# Revit family: HERZ-Herzcules-Thermostatkopf M28x1.5 9860
name_source: partatom
category: Rohrzubehör
units: mm (PartAtom-declared; Revit-internal decimal feet)

## family parameters
Arbeitsebenenbasiert = Nein
Beim Laden mit Abzugskörper schneiden = Nein
Bemaßung runder Anschluss = Durchmesser verwenden
Gemeinsam genutzt = Nein
Immer vertikal = Nein
OmniClass-Nummer = 23.65.55.14
OmniClass-Titel = Valves for Liquid Services
Teiletyp = Normal

## types (1)
- HERZ-Herzcules-Thermostatkopf M28x1.5 9860
    Anwendungen = HERZCULES, Thermostatkopf zur Montage auf HERZ-Ventilen, die für thermostatischen Betrieb eingerichtet sind.
    Ausführungen = HERZCULES, Heizkörperthermostat in Massivausführung
gegen Vandalismus, Diebstahl und unbefugte Betätigung.
Montage, Demontage und Sollwerteinstellung nur mit Spezialwerkzeugen möglich.
Sollwerteinstellung verriegelt, Einstellanzeige bleibt in verriegelter Position verdeckt.
Mit automatischer Frostsicherung.
    Bestellnummer = 1986010
    Funktionsweise = Der HERZ-Thermostat dient als Fühl- und Regelelement.
Durch die Volumsänderung der Flüssigkeitsfüllung im HERZ-Hydrosensor wird die Schubspindel des Ventils bewegt.
    Handrad = Kunststoff, weiß
    Hersteller = HERZ Armaturen Ges.m.b.H.
    S01 = 81 mm  [stored 0.265748 ft]
    S02 = 60 mm  [stored 0.19685 ft]
    Sollwertbereich = 8 - 26°C
    URL = www.herz-armaturen.at
    Vorgabe-Ansicht = 0 mm  [stored 0 ft]

note: [stored X ft] marks values corroborated as IEEE doubles in the binary element streams (Revit-internal decimal feet)
